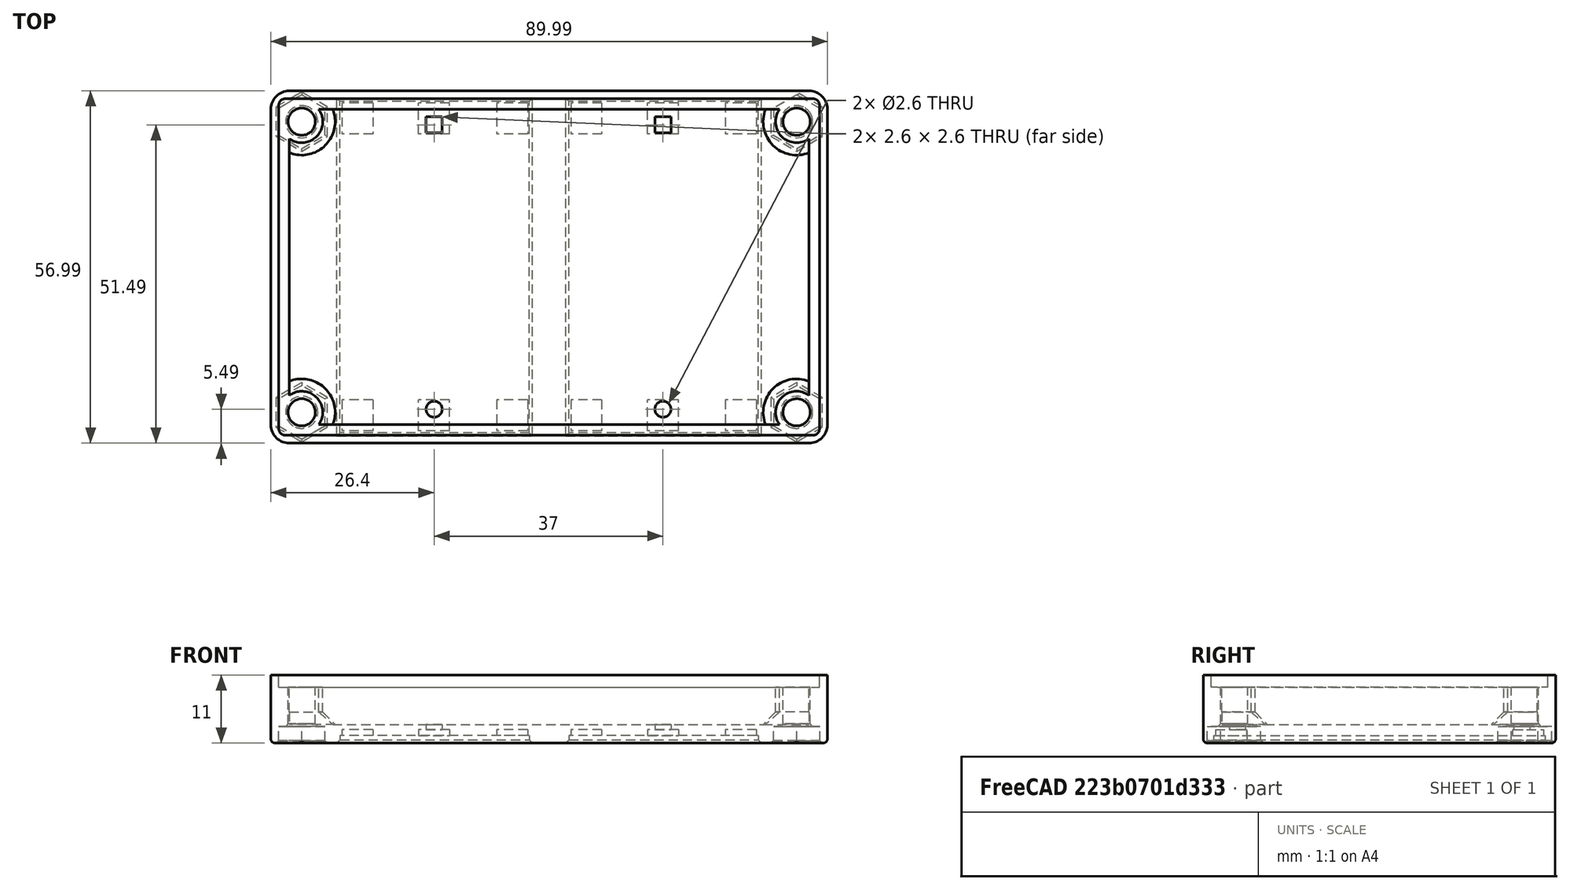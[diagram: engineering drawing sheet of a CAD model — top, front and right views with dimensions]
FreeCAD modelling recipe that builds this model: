
FCSTD DOCUMENT  (FreeCAD 0.18.4R)
Label: BoxTopGateway
License: All rights reserved
LicenseURL: http://en.wikipedia.org/wiki/All_rights_reserved
objects: Part::Box×23, Part::Cylinder×14, Part::Cut×11, Part::MultiFuse×7, Part::Chamfer×7, Sketcher::SketchObject×5, PartDesign::Pad×5, Part::Fillet×2, Mesh::Feature×1
note: 79 computed .brp shape members not serialized (recipe doc carries the construction recipe); baked Part::Feature solids carry a one-line shape summary decoded from their .brp

FEATURE [Sketcher::SketchObject] Sketch002
  MapMode = 5
  sketch-geometry (8):
    g0: LineSegment StartX=14.0007 StartY=-27.9902 StartZ=0 EndX=-70.009 EndY=-27.9902 EndZ=0
    g1: LineSegment StartX=-73 StartY=-24.9992 StartZ=0 EndX=-73 EndY=26 EndZ=0
    g2: LineSegment StartX=-70.0037 StartY=28.9963 StartZ=0 EndX=14.0188 EndY=28.9963 EndZ=0
    g3: LineSegment StartX=16.9862 StartY=26.0289 StartZ=0 EndX=16.9862 EndY=-25.0047 EndZ=0
    g4: ArcOfCircle CenterX=14.0007 CenterY=-25.0047 CenterZ=0 NormalX=0 NormalY=0 NormalZ=1 AngleXU=0 Radius=2.98549 StartAngle=4.71239 EndAngle=6.28319
    g5: ArcOfCircle CenterX=-70.009 CenterY=-24.9992 CenterZ=0 NormalX=0 NormalY=0 NormalZ=1 AngleXU=0 Radius=2.991 StartAngle=3.14159 EndAngle=4.71239
    g6: ArcOfCircle CenterX=-70.0037 CenterY=26 CenterZ=0 NormalX=0 NormalY=0 NormalZ=1 AngleXU=0 Radius=2.99626 StartAngle=1.5708 EndAngle=3.14159
    g7: ArcOfCircle CenterX=14.0188 CenterY=26.0289 CenterZ=0 NormalX=0 NormalY=0 NormalZ=1 AngleXU=0 Radius=2.96733 StartAngle=0 EndAngle=1.5708
  constraints (12):
    c: Horizontal(g0)
    c: Horizontal(g2)
    c: Vertical(g1)
    c: Vertical(g3)
    c: Tangent(g3,g4) = 1.5708
    c: Tangent(g0,g4) = 1.5708
    c: Tangent(g1,g5) = 1.5708
    c: Tangent(g0,g5) = 1.5708
    c: Tangent(g1,g6) = 1.5708
    c: Tangent(g2,g6) = 1.5708
    c: Tangent(g2,g7) = 1.5708
    c: Tangent(g3,g7) = 1.5708
FEATURE [PartDesign::Pad] Pad013
  Length = 12
  Length2 = 100
  Profile = -> Sketch002
  Type = 0
FEATURE [Part::Box] Box010  label="Würfel010"
  AttacherType = Attacher::AttachEngine3D
  Height = 25
  Length = 84
  Placement = pos=(-70,-25,3) rot=(0,0,1;0rad)
  Width = 51
FEATURE [Part::Cut] Cut011
  Base = -> Pad013
  Tool = -> Box010
FEATURE [Part::Box] Box  label="Rand002"
  AttacherType = Attacher::AttachEngine3D
  Height = 2
  Length = 87.4
  Placement = pos=(-71.7,25.7,14) rot=(0,0,1;0rad)
  Width = 2
FEATURE [Part::Box] Box011  label="Rand001"
  AttacherType = Attacher::AttachEngine3D
  Height = 2
  Length = 87.4
  Placement = pos=(-71.7,-26.7,14) rot=(0,0,1;0rad)
  Width = 2
FEATURE [Part::Box] Box012  label="Rand003"
  AttacherType = Attacher::AttachEngine3D
  Height = 2
  Length = 2
  Placement = pos=(-71.7,-25,14) rot=(0,0,1;0rad)
  Width = 51
FEATURE [Part::Box] Box013  label="Rand004"
  AttacherType = Attacher::AttachEngine3D
  Height = 2
  Length = 2
  Placement = pos=(13.7,-25,14) rot=(0,0,1;0rad)
  Width = 51
FEATURE [Part::MultiFuse] Fusion  label="RandFraesung"
  Placement = pos=(0,0,-4) rot=(0,0,1;0rad)
  Shapes = -> [Box013,Box012,Box011,Box]
FEATURE [Part::Cut] Cut  label="DeckelRaw"
  Base = -> Cut011
  Tool = -> Fusion
FEATURE [Part::Cylinder] Cylinder004  label="Zylinder002"
  Angle = 360
  AttacherType = Attacher::AttachEngine3D
  Height = 10
  Radius = 3.4
FEATURE [Part::Cylinder] Cylinder  label="Zylinder001"
  Angle = 360
  AttacherType = Attacher::AttachEngine3D
  Height = 10
  Radius = 2.2
FEATURE [Part::Cut] Cut027  label="Dom001"
  Base = -> Cylinder004
  Placement = pos=(12,-23,0) rot=(0,0,1;0rad)
  Tool = -> Cylinder
FEATURE [Part::Cylinder] Cylinder015  label="Zylinder015"
  Angle = 360
  AttacherType = Attacher::AttachEngine3D
  Height = 10
  Radius = 3.4
FEATURE [Part::Cylinder] Cylinder016  label="Zylinder016"
  Angle = 360
  AttacherType = Attacher::AttachEngine3D
  Height = 10
  Radius = 2.2
FEATURE [Part::Cut] Cut028  label="Dom002"
  Base = -> Cylinder015
  Placement = pos=(-68,-23,0) rot=(0,0,1;0rad)
  Tool = -> Cylinder016
FEATURE [Part::Cylinder] Cylinder017  label="Zylinder017"
  Angle = 360
  AttacherType = Attacher::AttachEngine3D
  Height = 10
  Radius = 3.4
FEATURE [Part::Cylinder] Cylinder018  label="Zylinder018"
  Angle = 360
  AttacherType = Attacher::AttachEngine3D
  Height = 10
  Radius = 2.2
FEATURE [Part::Cut] Cut029  label="Dom003"
  Base = -> Cylinder017
  Placement = pos=(-68,24,0) rot=(0,0,1;0rad)
  Tool = -> Cylinder018
FEATURE [Part::Cylinder] Cylinder019  label="Zylinder019"
  Angle = 360
  AttacherType = Attacher::AttachEngine3D
  Height = 10
  Radius = 3.4
FEATURE [Part::Cylinder] Cylinder020  label="Zylinder020"
  Angle = 360
  AttacherType = Attacher::AttachEngine3D
  Height = 10
  Radius = 2.2
FEATURE [Part::Cut] Cut030  label="Dom004"
  Base = -> Cylinder019
  Placement = pos=(12,24,0) rot=(0,0,1;0rad)
  Tool = -> Cylinder020
FEATURE [Part::MultiFuse] Fusion001  label="DeckelMitDomen"
  Shapes = -> [Cut,Cut027,Cut028,Cut029,Cut030]
FEATURE [Part::Cylinder] Cylinder021  label="DeckelBohrung001"
  Angle = 360
  AttacherType = Attacher::AttachEngine3D
  Height = 10
  Placement = pos=(12,-23,0) rot=(0,0,1;0rad)
  Radius = 2.2
FEATURE [Part::Cylinder] Cylinder022  label="DeckelBohrung002"
  Angle = 360
  AttacherType = Attacher::AttachEngine3D
  Height = 10
  Placement = pos=(-68,-23,0) rot=(0,0,1;0rad)
  Radius = 2.2
FEATURE [Part::Cylinder] Cylinder023  label="DeckelBohrung003"
  Angle = 360
  AttacherType = Attacher::AttachEngine3D
  Height = 10
  Placement = pos=(-68,24,0) rot=(0,0,1;0rad)
  Radius = 2.2
FEATURE [Part::Cylinder] Cylinder024  label="DeckelBohrung004"
  Angle = 360
  AttacherType = Attacher::AttachEngine3D
  Height = 10
  Placement = pos=(12,24,0) rot=(0,0,1;0rad)
  Radius = 2.2
FEATURE [Part::MultiFuse] Fusion002  label="DeckelBohrungen"
  Shapes = -> [Cylinder021,Cylinder022,Cylinder023,Cylinder024]
FEATURE [Part::Cut] Cut031  label="DomeDeckelGebohrt"
  Base = -> Fusion001
  Tool = -> Fusion002
FEATURE [Sketcher::SketchObject] Sketch001
  MapMode = 5
  Placement = pos=(12,-23,0) rot=(0,0,1;0.523599rad)
  sketch-geometry (7):
    g0: LineSegment StartX=4.32745 StartY=0.001167 StartZ=0 EndX=2.16272 EndY=3.74827 EndZ=0
    g1: LineSegment StartX=2.16272 StartY=3.74827 StartZ=0 EndX=-2.16474 EndY=3.7471 EndZ=0
    g2: LineSegment StartX=-2.16474 StartY=3.7471 StartZ=0 EndX=-4.32745 EndY=-0.001167 EndZ=0
    g3: LineSegment StartX=-4.32745 StartY=-0.001167 StartZ=0 EndX=-2.16272 EndY=-3.74827 EndZ=0
    g4: LineSegment StartX=-2.16272 StartY=-3.74827 StartZ=0 EndX=2.16474 EndY=-3.7471 EndZ=0
    g5: LineSegment StartX=2.16474 StartY=-3.7471 StartZ=0 EndX=4.32745 EndY=0.001167 EndZ=0
    g6: Circle [constr] CenterX=0 CenterY=0 CenterZ=0 NormalX=0 NormalY=0 NormalZ=1 AngleXU=0 Radius=4.32745
  constraints (13):
    c: Coincident(g0,g1)
    c: Coincident(g1,g2)
    c: Coincident(g2,g3)
    c: Coincident(g3,g4)
    c: Coincident(g4,g5)
    c: Coincident(g5,g0)
    c: Equal(g0, g1-g5) x5
    c: PointOnObject(g0,g6)
    c: PointOnObject(g1,g6)
    c: PointOnObject(g2,g6)
    c: PointOnObject(g3,g6)
    c: PointOnObject(g4,g6)
    c: PointOnObject(g5,g6)
FEATURE [PartDesign::Pad] Pad  label="ScrewNut001"
  Length = 2.7
  Length2 = 100
  Placement = pos=(12,-23,0) rot=(0,0,1;0.523599rad)
  Profile = -> Sketch001
  Type = 0
FEATURE [Sketcher::SketchObject] Sketch003
  MapMode = 5
  Placement = pos=(-68,-23,0) rot=(0,0,1;0.523599rad)
  sketch-geometry (7):
    g0: LineSegment StartX=4.32745 StartY=0.001167 StartZ=0 EndX=2.16272 EndY=3.74827 EndZ=0
    g1: LineSegment StartX=2.16272 StartY=3.74827 StartZ=0 EndX=-2.16474 EndY=3.7471 EndZ=0
    g2: LineSegment StartX=-2.16474 StartY=3.7471 StartZ=0 EndX=-4.32745 EndY=-0.001167 EndZ=0
    g3: LineSegment StartX=-4.32745 StartY=-0.001167 StartZ=0 EndX=-2.16272 EndY=-3.74827 EndZ=0
    g4: LineSegment StartX=-2.16272 StartY=-3.74827 StartZ=0 EndX=2.16474 EndY=-3.7471 EndZ=0
    g5: LineSegment StartX=2.16474 StartY=-3.7471 StartZ=0 EndX=4.32745 EndY=0.001167 EndZ=0
    g6: Circle [constr] CenterX=0 CenterY=0 CenterZ=0 NormalX=0 NormalY=0 NormalZ=1 AngleXU=0 Radius=4.32745
  constraints (13):
    c: Coincident(g0,g1)
    c: Coincident(g1,g2)
    c: Coincident(g2,g3)
    c: Coincident(g3,g4)
    c: Coincident(g4,g5)
    c: Coincident(g5,g0)
    c: Equal(g0, g1-g5) x5
    c: PointOnObject(g0,g6)
    c: PointOnObject(g1,g6)
    c: PointOnObject(g2,g6)
    c: PointOnObject(g3,g6)
    c: PointOnObject(g4,g6)
    c: PointOnObject(g5,g6)
FEATURE [PartDesign::Pad] Pad014  label="ScrewNut002"
  Length = 2.7
  Length2 = 100
  Placement = pos=(-68,-23,0) rot=(0,0,1;0.523599rad)
  Profile = -> Sketch003
  Type = 0
FEATURE [Sketcher::SketchObject] Sketch004
  MapMode = 5
  Placement = pos=(-68,24,0) rot=(0,0,1;0.523599rad)
  sketch-geometry (7):
    g0: LineSegment StartX=4.32745 StartY=0.001167 StartZ=0 EndX=2.16272 EndY=3.74827 EndZ=0
    g1: LineSegment StartX=2.16272 StartY=3.74827 StartZ=0 EndX=-2.16474 EndY=3.7471 EndZ=0
    g2: LineSegment StartX=-2.16474 StartY=3.7471 StartZ=0 EndX=-4.32745 EndY=-0.001167 EndZ=0
    g3: LineSegment StartX=-4.32745 StartY=-0.001167 StartZ=0 EndX=-2.16272 EndY=-3.74827 EndZ=0
    g4: LineSegment StartX=-2.16272 StartY=-3.74827 StartZ=0 EndX=2.16474 EndY=-3.7471 EndZ=0
    g5: LineSegment StartX=2.16474 StartY=-3.7471 StartZ=0 EndX=4.32745 EndY=0.001167 EndZ=0
    g6: Circle [constr] CenterX=0 CenterY=0 CenterZ=0 NormalX=0 NormalY=0 NormalZ=1 AngleXU=0 Radius=4.32745
  constraints (13):
    c: Coincident(g0,g1)
    c: Coincident(g1,g2)
    c: Coincident(g2,g3)
    c: Coincident(g3,g4)
    c: Coincident(g4,g5)
    c: Coincident(g5,g0)
    c: Equal(g0, g1-g5) x5
    c: PointOnObject(g0,g6)
    c: PointOnObject(g1,g6)
    c: PointOnObject(g2,g6)
    c: PointOnObject(g3,g6)
    c: PointOnObject(g4,g6)
    c: PointOnObject(g5,g6)
FEATURE [PartDesign::Pad] Pad015  label="ScrewNut003"
  Length = 2.7
  Length2 = 100
  Placement = pos=(-68,24,0) rot=(0,0,1;0.523599rad)
  Profile = -> Sketch004
  Type = 0
FEATURE [Sketcher::SketchObject] Sketch005
  MapMode = 5
  Placement = pos=(12,24,0) rot=(0,0,1;0.523599rad)
  sketch-geometry (7):
    g0: LineSegment StartX=4.32745 StartY=0.001167 StartZ=0 EndX=2.16272 EndY=3.74827 EndZ=0
    g1: LineSegment StartX=2.16272 StartY=3.74827 StartZ=0 EndX=-2.16474 EndY=3.7471 EndZ=0
    g2: LineSegment StartX=-2.16474 StartY=3.7471 StartZ=0 EndX=-4.32745 EndY=-0.001167 EndZ=0
    g3: LineSegment StartX=-4.32745 StartY=-0.001167 StartZ=0 EndX=-2.16272 EndY=-3.74827 EndZ=0
    g4: LineSegment StartX=-2.16272 StartY=-3.74827 StartZ=0 EndX=2.16474 EndY=-3.7471 EndZ=0
    g5: LineSegment StartX=2.16474 StartY=-3.7471 StartZ=0 EndX=4.32745 EndY=0.001167 EndZ=0
    g6: Circle [constr] CenterX=0 CenterY=0 CenterZ=0 NormalX=0 NormalY=0 NormalZ=1 AngleXU=0 Radius=4.32745
  constraints (13):
    c: Coincident(g0,g1)
    c: Coincident(g1,g2)
    c: Coincident(g2,g3)
    c: Coincident(g3,g4)
    c: Coincident(g4,g5)
    c: Coincident(g5,g0)
    c: Equal(g0, g1-g5) x5
    c: PointOnObject(g0,g6)
    c: PointOnObject(g1,g6)
    c: PointOnObject(g2,g6)
    c: PointOnObject(g3,g6)
    c: PointOnObject(g4,g6)
    c: PointOnObject(g5,g6)
FEATURE [PartDesign::Pad] Pad016  label="ScrewNut004"
  Length = 2.7
  Length2 = 100
  Placement = pos=(12,24,0) rot=(0,0,1;0.523599rad)
  Profile = -> Sketch005
  Type = 0
FEATURE [Part::Box] Box015  label="Würfel014"
  AttacherType = Attacher::AttachEngine3D
  Height = 1.1
  Length = 5
  Placement = pos=(-15,-26,4) rot=(0,0,1;0rad)
  Width = 5
FEATURE [Part::Box] Box016  label="Würfel015"
  AttacherType = Attacher::AttachEngine3D
  Height = 1.1
  Length = 5
  Placement = pos=(10,-26,4) rot=(0,0,1;0rad)
  Width = 5
FEATURE [Part::Box] Box017  label="Würfel016"
  AttacherType = Attacher::AttachEngine3D
  Height = 1.1
  Length = 5
  Placement = pos=(-15,22,4) rot=(0,0,1;0rad)
  Width = 5
FEATURE [Part::Box] Box018  label="Würfel017"
  AttacherType = Attacher::AttachEngine3D
  Height = 1.1
  Length = 5
  Placement = pos=(10,22,4) rot=(0,0,1;0rad)
  Width = 5
FEATURE [Part::Box] Box019  label="Würfel018"
  AttacherType = Attacher::AttachEngine3D
  Height = 2
  Length = 30.6
  Placement = pos=(-15.3,-26.3,5) rot=(0,0,1;0rad)
  Width = 53.6
FEATURE [Part::Box] Box020  label="Würfel019"
  AttacherType = Attacher::AttachEngine3D
  Height = 1.1
  Length = 5
  Placement = pos=(-2.4,22,4) rot=(0,0,1;0rad)
  Width = 5
FEATURE [Part::Box] Box021  label="Würfel020"
  AttacherType = Attacher::AttachEngine3D
  Height = 1.1
  Length = 5
  Placement = pos=(-2.4,-26,4) rot=(0,0,1;0rad)
  Width = 5
FEATURE [Part::Box] Box022  label="Würfel021"
  AttacherType = Attacher::AttachEngine3D
  Height = 4.1
  Length = 2.6
  Placement = pos=(-1.2,22.2,0) rot=(0,0,1;0rad)
  Width = 2.6
FEATURE [Part::Cylinder] Cylinder025  label="Zylinder021"
  Angle = 360
  AttacherType = Attacher::AttachEngine3D
  Height = 5.1
  Placement = pos=(0.1,-22.5,0) rot=(0,0,1;0rad)
  Radius = 1.3
FEATURE [Part::MultiFuse] Fusion004  label="CellCut002"
  Placement = pos=(19,0,0) rot=(0,1,0;3.14159rad)
  Shapes = -> [Cylinder025,Box017,Box015,Box016,Box018,Box019,Box020,Box021,Box022]
FEATURE [Part::Box] Box023  label="Würfel022"
  AttacherType = Attacher::AttachEngine3D
  Height = 1.1
  Length = 5
  Placement = pos=(-15,-26,4) rot=(0,0,1;0rad)
  Width = 5
FEATURE [Part::Box] Box024  label="Würfel023"
  AttacherType = Attacher::AttachEngine3D
  Height = 1.1
  Length = 5
  Placement = pos=(10,-26,4) rot=(0,0,1;0rad)
  Width = 5
FEATURE [Part::Box] Box025  label="Würfel024"
  AttacherType = Attacher::AttachEngine3D
  Height = 1.1
  Length = 5
  Placement = pos=(-15,22,4) rot=(0,0,1;0rad)
  Width = 5
FEATURE [Part::Box] Box026  label="Würfel025"
  AttacherType = Attacher::AttachEngine3D
  Height = 1.1
  Length = 5
  Placement = pos=(10,22,4) rot=(0,0,1;0rad)
  Width = 5
FEATURE [Part::Box] Box027  label="Würfel026"
  AttacherType = Attacher::AttachEngine3D
  Height = 2
  Length = 30.6
  Placement = pos=(-15.3,-26.3,5) rot=(0,0,1;0rad)
  Width = 53.6
FEATURE [Part::Box] Box028  label="Würfel027"
  AttacherType = Attacher::AttachEngine3D
  Height = 1.1
  Length = 5
  Placement = pos=(-2.4,22,4) rot=(0,0,1;0rad)
  Width = 5
FEATURE [Part::Box] Box029  label="Würfel028"
  AttacherType = Attacher::AttachEngine3D
  Height = 1.1
  Length = 5
  Placement = pos=(-2.4,-26,4) rot=(0,0,1;0rad)
  Width = 5
FEATURE [Part::Box] Box030  label="Würfel029"
  AttacherType = Attacher::AttachEngine3D
  Height = 4.1
  Length = 2.6
  Placement = pos=(-1.2,22.2,0) rot=(0,0,1;0rad)
  Width = 2.6
FEATURE [Part::Cylinder] Cylinder026  label="Zylinder022"
  Angle = 360
  AttacherType = Attacher::AttachEngine3D
  Height = 5.1
  Placement = pos=(0.1,-22.5,0) rot=(0,0,1;0rad)
  Radius = 1.3
FEATURE [Part::MultiFuse] Fusion005  label="CellCut001"
  Placement = pos=(-18,0,0) rot=(0,1,0;3.14159rad)
  Shapes = -> [Cylinder026,Box025,Box023,Box024,Box026,Box027,Box028,Box029,Box030]
FEATURE [Part::MultiFuse] Fusion006  label="CellCut"
  Placement = pos=(-28.5,0,6.2) rot=(0,0,1;0rad)
  Shapes = -> [Fusion004,Fusion005]
FEATURE [Part::MultiFuse] Fusion007  label="ScrewNuts"
  Shapes = -> [Pad,Pad014,Pad015,Pad016]
FEATURE [Part::Cut] Cut032
  Base = -> Cut031
  Tool = -> Fusion006
FEATURE [Part::Chamfer] Chamfer
  Base = -> Cut032
  Edges = 8 edges r=0.5: [Edge18,Edge19,Edge20,Edge21,Edge22,Edge23,Edge24,Edge25]
FEATURE [Part::Fillet] Fillet
  Base = -> Chamfer
  Edges = 8 edges r=0.7: [Edge5,Edge6,Edge7,Edge8,Edge9,Edge10,Edge11,Edge12]
FEATURE [Part::Cut] Cut033
  Base = -> Fillet
  Tool = -> Fusion007
FEATURE [Part::Chamfer] Chamfer001
  Base = -> Cut033
  Edges = 1 edges r=0.4: [Edge139]
FEATURE [Part::Chamfer] Chamfer002
  Base = -> Chamfer001
  Edges = 1 edges r=0.4: [Edge202]
FEATURE [Part::Chamfer] Chamfer003
  Base = -> Chamfer002
  Edges = 1 edges r=0.4: [Edge207]
FEATURE [Part::Chamfer] Chamfer004
  Base = -> Chamfer003
  Edges = 1 edges r=0.4: [Edge195]
FEATURE [Part::Chamfer] Chamfer005
  Base = -> Chamfer004
  Edges = 23 edges r=0.4: [Edge22,Edge27,Edge32,Edge33,Edge35,Edge49,Edge50,Edge51,Edge52,Edge53,Edge54,Edge60,Edge61,Edge62,Edge63,Edge64,Edge65,Edge67,Edge68,Edge69,Edge70,Edge71,Edge72]
FEATURE [Part::Box] Box031  label="Würfel"
  AttacherType = Attacher::AttachEngine3D
  Height = 1
  Length = 87.4
  Placement = pos=(-71.7,-26.7,9) rot=(0,0,1;0rad)
  Width = 54.4
FEATURE [Part::Cut] Cut034
  Base = -> Chamfer005
  Tool = -> Box031
FEATURE [Part::Box] Box032  label="Würfel030"
  AttacherType = Attacher::AttachEngine3D
  Height = 1
  Length = 91
  Placement = pos=(-73.5,-28.5,11) rot=(0,0,1;0rad)
  Width = 58
FEATURE [Part::Cut] Cut035
  Base = -> Cut034
  Tool = -> Box032
FEATURE [Part::Chamfer] Chamfer006
  Base = -> Cut035
  Edges = 6 edges r=2: [Edge398,Edge400,Edge404,Edge406,Edge410,Edge414]
FEATURE [Part::Fillet] Fillet001
  Base = -> Chamfer006
  Edges = 4 edges r=1: [Edge159,Edge163,Edge168,Edge170]
FEATURE [Mesh::Feature] Mesh  label="Fillet001 (Meshed)"
